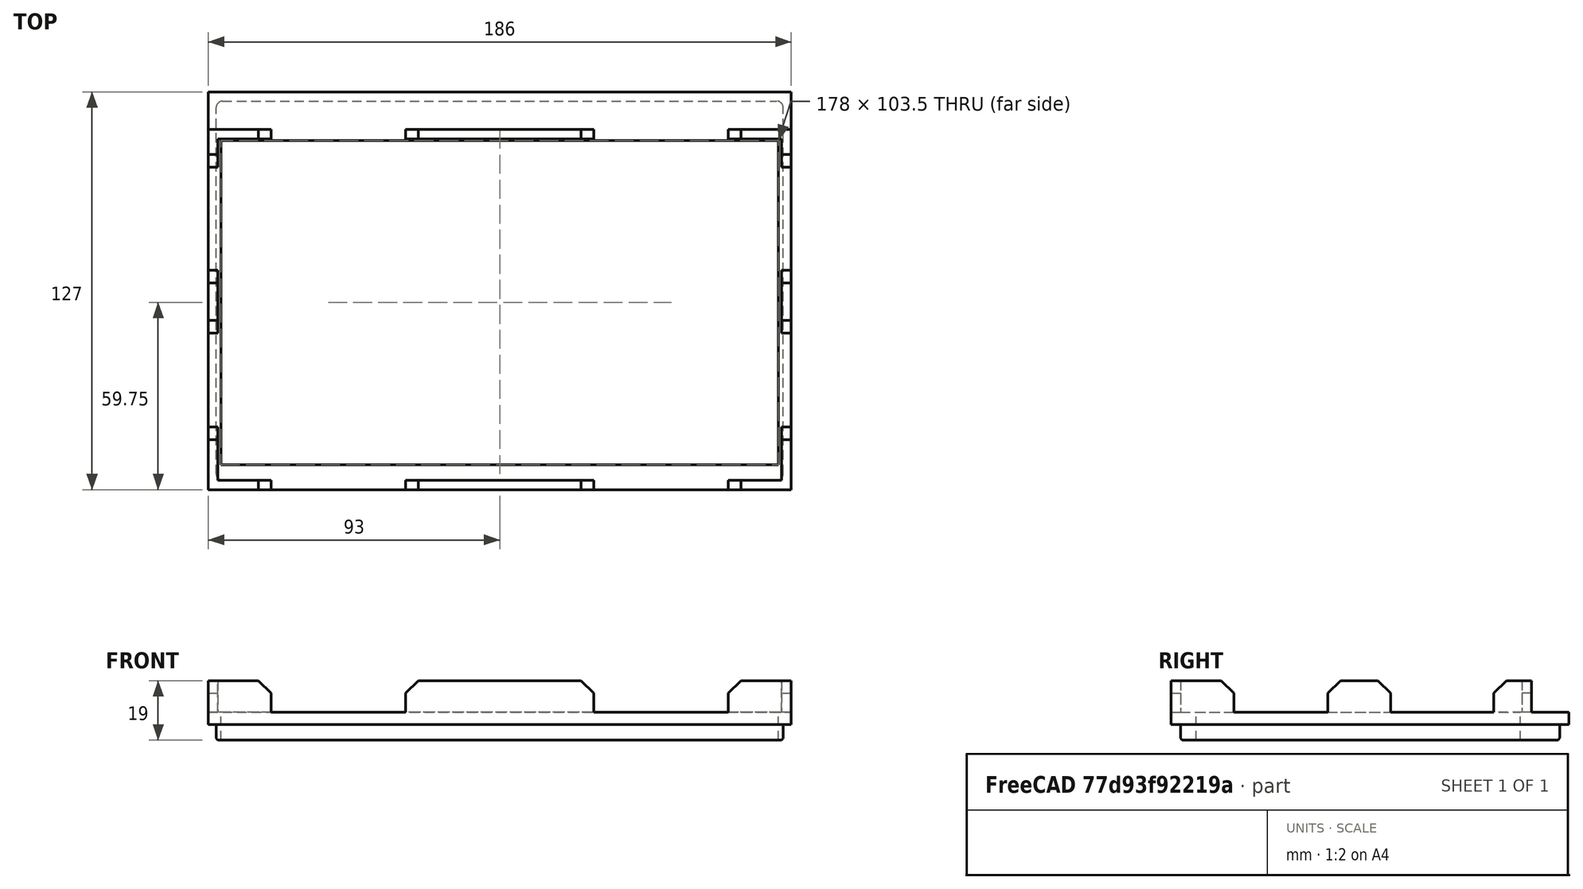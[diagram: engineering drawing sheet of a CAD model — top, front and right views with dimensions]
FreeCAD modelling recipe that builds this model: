
FCSTD DOCUMENT  (FreeCAD 0.20R29177 (Git))
Label: fascia-joying
License: All rights reserved
LicenseURL: http://en.wikipedia.org/wiki/All_rights_reserved
objects: Part::Box×16, Part::Cut×6, Part::MultiFuse×5, Part::Fillet×2, Part::Chamfer×1
note: 30 computed .brp shape members not serialized (recipe doc carries the construction recipe); baked Part::Feature solids carry a one-line shape summary decoded from their .brp

FEATURE [Part::Box] Box017  label="Lip"
  AttacherType = Attacher::AttachEngine3D
  Height = 4
  Length = 186
  Width = 127
FEATURE [Part::Box] Box018  label="Cutout"
  AttacherType = Attacher::AttachEngine3D
  Height = 30
  Length = 178
  Placement = pos=(4,8,-25) rot=(0,0,1;0rad)
  Width = 103.5
FEATURE [Part::Box] Box019  label="Cube016"
  AttacherType = Attacher::AttachEngine3D
  Height = 5
  Length = 181
  Placement = pos=(2.5,3,-5) rot=(0,0,1;0rad)
  Width = 121
FEATURE [Part::MultiFuse] Fusion007
  Shapes = -> [Box017,Box019]
FEATURE [Part::Cut] Cut007
  Base = -> Fusion007
  Tool = -> Box018
FEATURE [Part::Fillet] Fillet008  label="Fill Plate"
  Base = -> Cut007
  Edges = 4 edges r=2: [Edge30,Edge31,Edge32,Edge35]
FEATURE [Part::Box] Box021  label="Cube018"
  AttacherType = Attacher::AttachEngine3D
  Height = 11
  Length = 20
  Width = 20
FEATURE [Part::Box] Box022  label="Cube019"
  AttacherType = Attacher::AttachEngine3D
  Height = 11
  Length = 30
  Placement = pos=(3,3,0) rot=(0,0,1;0rad)
  Width = 20
FEATURE [Part::Cut] Cut009
  Base = -> Box021
  Placement = pos=(0,0,4) rot=(0,0,1;0rad)
  Tool = -> Box022
FEATURE [Part::Box] Box023  label="Cube020"
  AttacherType = Attacher::AttachEngine3D
  Height = 11
  Length = 20
  Width = 20
FEATURE [Part::Box] Box024  label="Cube021"
  AttacherType = Attacher::AttachEngine3D
  Height = 11
  Length = 30
  Placement = pos=(3,3,0) rot=(0,0,1;0rad)
  Width = 20
FEATURE [Part::Cut] Cut010
  Base = -> Box023
  Placement = pos=(186,0,15) rot=(0,1,0;3.14159rad)
  Tool = -> Box024
FEATURE [Part::Box] Box025  label="Cube022"
  AttacherType = Attacher::AttachEngine3D
  Height = 11
  Length = 3
  Placement = pos=(0,50,4) rot=(0,0,1;0rad)
  Width = 20
FEATURE [Part::Box] Box026  label="Cube023"
  AttacherType = Attacher::AttachEngine3D
  Height = 11
  Length = 3
  Placement = pos=(183,50,4) rot=(0,0,1;0rad)
  Width = 20
FEATURE [Part::Box] Box029  label="Cube026"
  AttacherType = Attacher::AttachEngine3D
  Height = 11
  Length = 20
  Width = 20
FEATURE [Part::Box] Box030  label="Cube027"
  AttacherType = Attacher::AttachEngine3D
  Height = 11
  Length = 30
  Placement = pos=(3,3,0) rot=(0,0,1;0rad)
  Width = 20
FEATURE [Part::Cut] Cut012
  Base = -> Box029
  Placement = pos=(0,115,15) rot=(1,0,0;3.14159rad)
  Tool = -> Box030
FEATURE [Part::Box] Box031  label="Cube028"
  AttacherType = Attacher::AttachEngine3D
  Height = 11
  Length = 20
  Width = 20
FEATURE [Part::Box] Box032  label="Cube029"
  AttacherType = Attacher::AttachEngine3D
  Height = 11
  Length = 30
  Placement = pos=(3,3,0) rot=(0,0,1;0rad)
  Width = 20
FEATURE [Part::Cut] Cut013
  Base = -> Box031
  Placement = pos=(186,115,4) rot=(0,0,1;3.14159rad)
  Tool = -> Box032
FEATURE [Part::MultiFuse] Fusion014
  Shapes = -> [Cut009,Box025,Box026,Cut010,Cut013,Cut012]
FEATURE [Part::Box] Box033  label="Cube030"
  AttacherType = Attacher::AttachEngine3D
  Height = 11
  Length = 60
  Placement = pos=(63,112,4) rot=(0,0,1;0rad)
  Width = 3
FEATURE [Part::MultiFuse] Fusion015
  Shapes = -> [Fusion014,Box033]
FEATURE [Part::Fillet] Fillet009
  Base = -> Fillet008
  Edges = 8 edges r=1: [Edge13,Edge16,Edge18,Edge21,Edge23,Edge24,Edge26,Edge28]
FEATURE [Part::Box] Box034  label="Cube031"
  AttacherType = Attacher::AttachEngine3D
  Height = 20
  Length = 200
  Placement = pos=(-10,73,-5) rot=(0,0,1;0rad)
  Width = 30
FEATURE [Part::Cut] Cut014
  Base = -> Fusion015
  Tool = -> Box034
FEATURE [Part::Box] Box035  label="Cube032"
  AttacherType = Attacher::AttachEngine3D
  Height = 11
  Length = 60
  Placement = pos=(63,0,4) rot=(0,0,1;0rad)
  Width = 3
FEATURE [Part::MultiFuse] Fusion016
  Shapes = -> [Cut014,Box035]
FEATURE [Part::Chamfer] Chamfer006
  Base = -> Fusion016
  Edges = 16 edges r=4: [Edge12,Edge16,Edge20,Edge24,Edge41,Edge44,Edge58,Edge60,Edge65,Edge68,Edge80,Edge84,Edge100,Edge102,Edge110,Edge113]
  Placement = pos=(0,0,-1) rot=(0,0,1;0rad)
FEATURE [Part::MultiFuse] Fusion017  label="Fascia (Modified)"
  Shapes = -> [Fillet009,Chamfer006]
